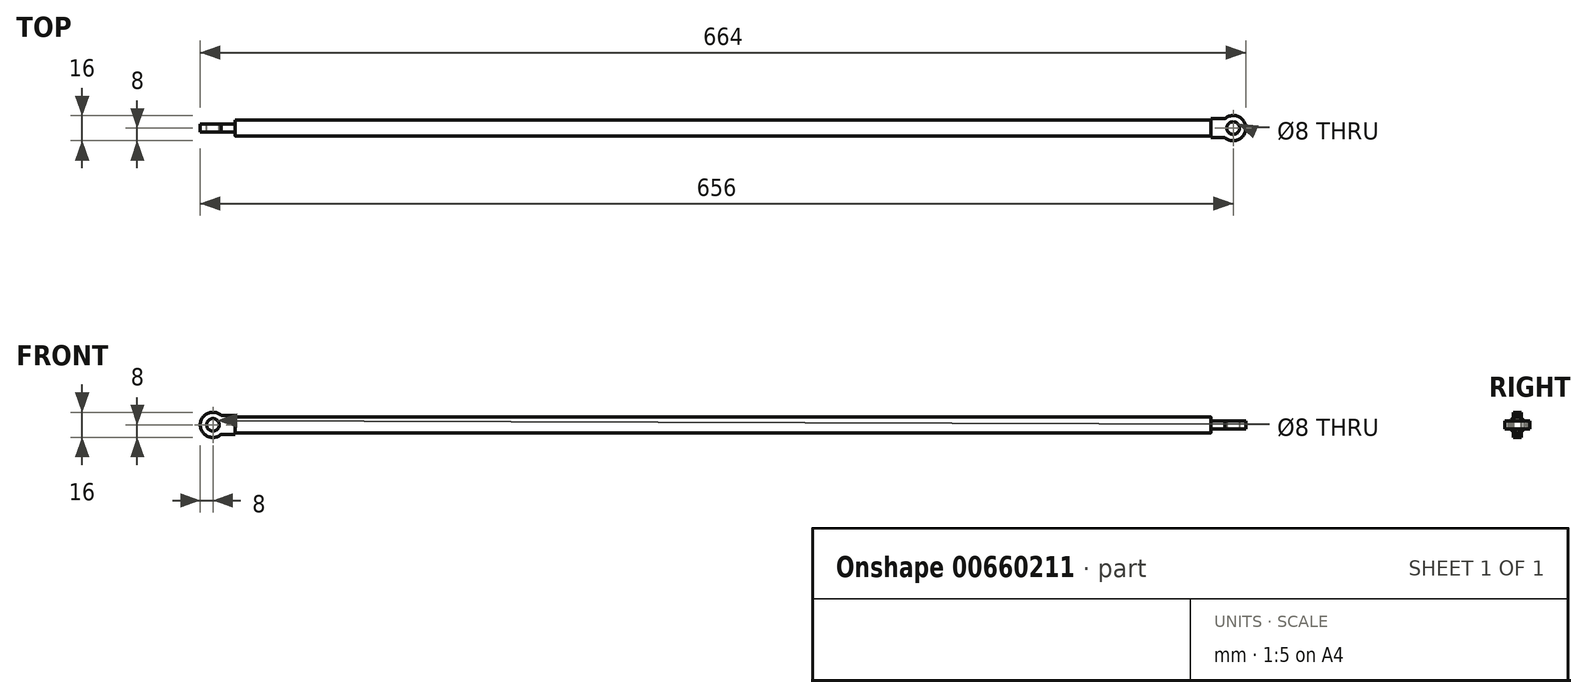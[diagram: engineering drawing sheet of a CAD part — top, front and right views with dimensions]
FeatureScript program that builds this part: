
annotation { "Feature Type Name" : "Feature", "Feature Type Description" : "" }
export const myFeature = defineFeature(function(context is Context, id is Id, definition is map)
    precondition{}
    {
        {
            var Q0;
            Q0=qCreatedBy(makeId("Right.planeOp"),FACE);
            var sketch = newSketch(context, id + "F0", { "sketchPlane" : qUnion([Q0])});
            skCircle(sketch, "E0", {"center": v(0, 0) * mm, "radius": 5 * mm});
            skSolve(sketch);
        }
        {
            var Q0;
            Q0 = qSketchRegion(id + "F0", true);
            extrude(context, id + "F1", {"entities" : qUnion([Q0]), "depth" : 620 * mm, "offsetDistance" : 25 * mm});
        }
        {
            var Q0;
            Q0=qCreatedBy(makeId("Front.planeOp"),FACE);
            var sketch = newSketch(context, id + "F2", { "sketchPlane" : qUnion([Q0])});
            skLineSegment(sketch, "E1.bottom", {"start": v(0, 6) * mm, "end": v(-8.7, 6) * mm});
            skLineSegment(sketch, "E1.top", {"start": v(0, -6) * mm, "end": v(-8.7, -6) * mm});
            skLineSegment(sketch, "E1.left", {"start": v(0, 6) * mm, "end": v(0, -6) * mm});
            skCircle(sketch, "E2", {"center": v(-14, 0) * mm, "radius": 4 * mm});
            skArc(sketch, "E3", {"start": v(-8.7, 6) * mm, "mid": v(-22, 0) * mm, "end": v(-8.7, -6) * mm});
            skSolve(sketch);
        }
        {
            var Q0;
            Q0 = qSketchRegion(id + "F2", true);
            extrude(context, id + "F3", {"entities" : qUnion([Q0]), "operationType" : NewBodyOperationType.ADD, "endBound" : BoundingType.SYMMETRIC, "depth" : 5 * mm, "offsetDistance" : 25 * mm});
        }
        {
            var Q0;
            Q0=qCreatedBy(makeId("Top.planeOp"),FACE);
            var sketch = newSketch(context, id + "F4", { "sketchPlane" : qUnion([Q0])});
            skLineSegment(sketch, "E4.bottom", {"start": v(620, 6) * mm, "end": v(628.7, 6) * mm});
            skLineSegment(sketch, "E4.top", {"start": v(620, -6) * mm, "end": v(628.7, -6) * mm});
            skLineSegment(sketch, "E4.left", {"start": v(620, 6) * mm, "end": v(620, -6) * mm});
            skCircle(sketch, "E5", {"center": v(634, 0) * mm, "radius": 4 * mm});
            skArc(sketch, "E6", {"start": v(628.7, -6) * mm, "mid": v(642, 0) * mm, "end": v(628.7, 6) * mm});
            skSolve(sketch);
        }
        {
            var Q0;
            Q0 = qSketchRegion(id + "F4", true);
            extrude(context, id + "F5", {"entities" : qUnion([Q0]), "operationType" : NewBodyOperationType.ADD, "endBound" : BoundingType.SYMMETRIC, "depth" : 5 * mm, "offsetDistance" : 25 * mm});
        }
    });
